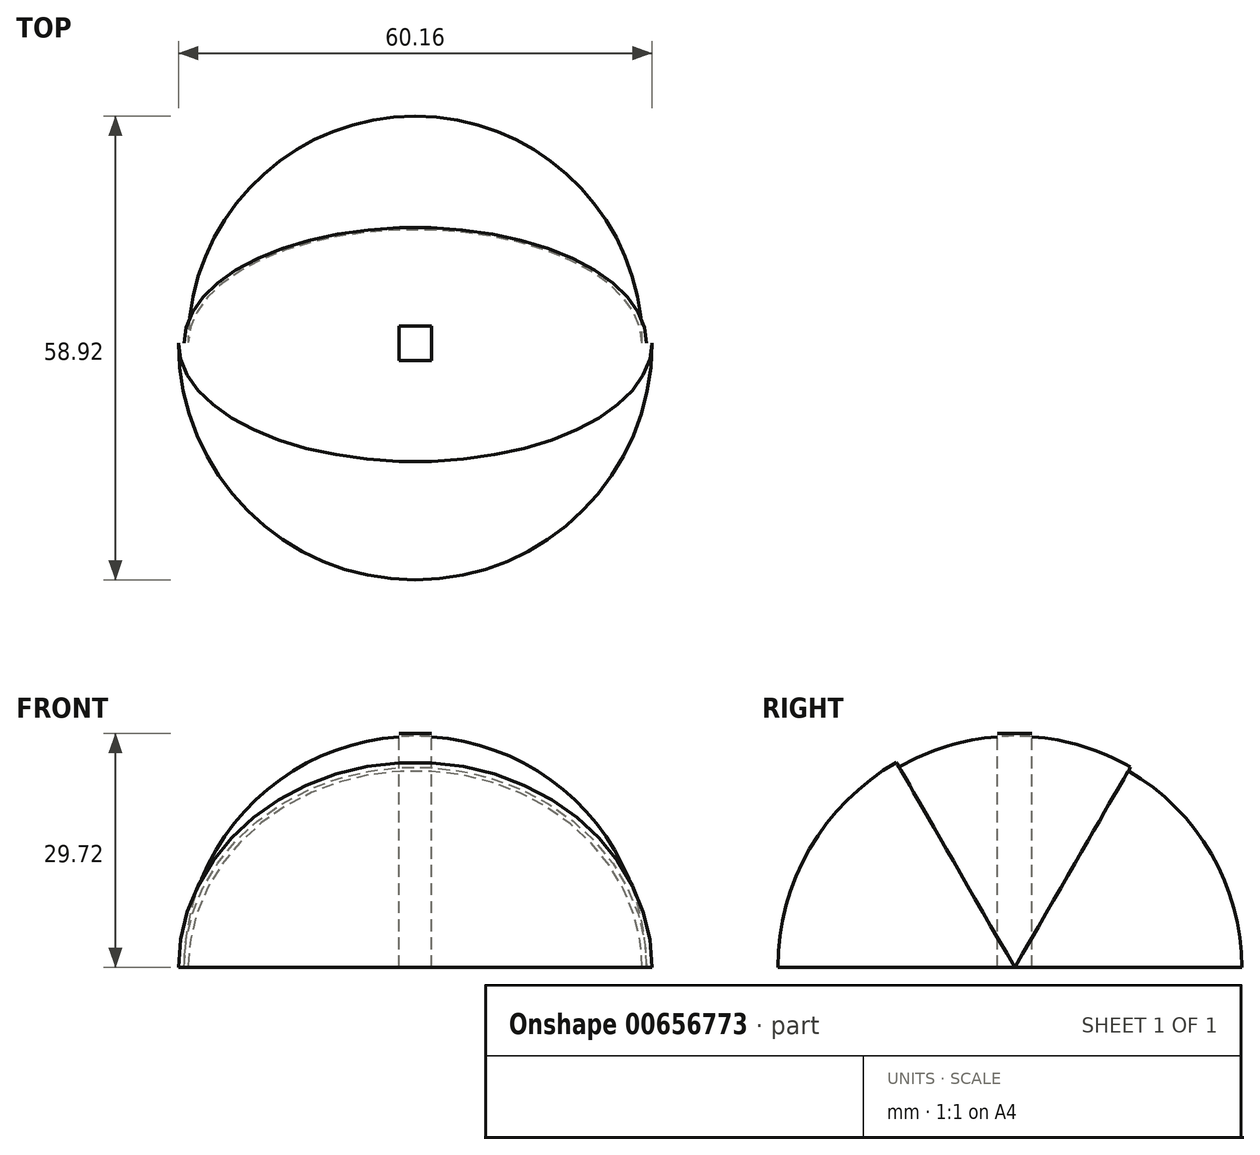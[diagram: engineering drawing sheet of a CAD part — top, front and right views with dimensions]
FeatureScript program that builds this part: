
annotation { "Feature Type Name" : "Feature", "Feature Type Description" : "" }
export const myFeature = defineFeature(function(context is Context, id is Id, definition is map)
    precondition{}
    {
        {
            var Q0;
            Q0=qCreatedBy(makeId("Top.planeOp"),FACE);
            var sketch = newSketch(context, id + "F0", { "sketchPlane" : qUnion([Q0])});
            skArc(sketch, "E0", {"start": v(-30.08, 0) * mm, "mid": v(0, -30.08) * mm, "end": v(30.08, 0) * mm});
            skLineSegment(sketch, "E1", {"start": v(30.08, 0) * mm, "end": v(-30.08, 0) * mm});
            skSolve(sketch);
        }
        {
            var Q0;
            Q0 = qSketchRegion(id + "F0", true);
            var Q1;
            Q1=sQuery(id+"F0.wireOp",EDGE,"E0");
            var Q2;
            Q2 = qBodyType(qCreatedBy(id + "F9tb82EHwottTsZ_0" ,EDGE), BodyType.WIRE);
            var Q3;
            Q3=sQuery(id+"F0.wireOp",EDGE,"E1");
            revolve(context, id + "F1", {"bodyType" : ToolBodyType.SURFACE, "entities" : qUnion([Q0]), "surfaceEntities" : qUnion([Q1, Q2]), "axis" : qUnion([Q3]), "revolveType" : RevolveType.ONE_DIRECTION, "angle" : 60 * degree});
        }
        {
            var Q0;
            Q0=qCreatedBy(makeId("Top.planeOp"),FACE);
            var sketch = newSketch(context, id + "F2", { "sketchPlane" : qUnion([Q0])});
            skArc(sketch, "E2", {"start": v(28.84, 0) * mm, "mid": v(0.1, 28.84) * mm, "end": v(-28.84, 0.2) * mm});
            skLineSegment(sketch, "E3", {"start": v(-28.84, 0.2) * mm, "end": v(28.84, 0) * mm});
            skSolve(sketch);
        }
        {
            var Q0;
            Q0=makeQuery(id+"F2.imprint","IMPRINT",FACE,{"disambiguationData":[TD([[makeQuery(id+"F2.imprint","IMPRINT",EDGE,{"derivedFrom":sQuery(id+"F2.wireOp",EDGE,"E2")}),1.0]])]});
            var Q1;
            Q1=sQuery(id+"F2.wireOp",EDGE,"E2");
            var Q2;
            Q2=sQuery(id+"F0.wireOp",EDGE,"E1");
            revolve(context, id + "F3", {"bodyType" : ToolBodyType.SURFACE, "entities" : qUnion([Q0]), "surfaceEntities" : qUnion([Q1]), "axis" : qUnion([Q2]), "revolveType" : RevolveType.ONE_DIRECTION, "oppositeDirection" : true, "angle" : 60 * degree});
        }
        {
            var Q0;
            Q0=qCreatedBy(makeId("Top.planeOp"),FACE);
            var sketch = newSketch(context, id + "F4", { "sketchPlane" : qUnion([Q0])});
            skLineSegment(sketch, "E4", {"start": v(29.67, 0) * mm, "end": v(-29.38, 0) * mm});
            skArc(sketch, "E5", {"start": v(-29.38, 0) * mm, "mid": v(0, -29.38) * mm, "end": v(29.38, 0) * mm});
            skSolve(sketch);
        }
        {
            var Q0;
            Q0 = qSketchRegion(id + "F4", true);
            var Q1;
            Q1=sQuery(id+"F4.wireOp",EDGE,"E5");
            var Q2;
            Q2=sQuery(id+"F0.wireOp",EDGE,"E1");
            revolve(context, id + "F5", {"bodyType" : ToolBodyType.SURFACE, "entities" : qUnion([Q0]), "surfaceEntities" : qUnion([Q1]), "axis" : qUnion([Q2]), "revolveType" : RevolveType.TWO_DIRECTIONS, "angle" : 120 * degree, "angleBack" : 60 * degree});
        }
        {
            var Q0;
            Q0=qCreatedBy(makeId("Top.planeOp"),FACE);
            var sketch = newSketch(context, id + "F6", { "sketchPlane" : qUnion([Q0])});
            skLineSegment(sketch, "E6.bottom", {"start": v(2.08, 2.18) * mm, "end": v(-2.08, 2.18) * mm});
            skLineSegment(sketch, "E6.top", {"start": v(2.08, -2.18) * mm, "end": v(-2.08, -2.18) * mm});
            skLineSegment(sketch, "E6.left", {"start": v(2.08, 2.18) * mm, "end": v(2.08, -2.18) * mm});
            skLineSegment(sketch, "E6.right", {"start": v(-2.08, 2.18) * mm, "end": v(-2.08, -2.18) * mm});
            skPoint(sketch, "E6.middle", {"position": v(0, 0) * mm});
            skSolve(sketch);
        }
        {
            var Q0;
            Q0 = qSketchRegion(id + "F6", true);
            var Q1;
            Q1 = qBodyType(qCreatedBy(id + "F6" ,EDGE), BodyType.WIRE);
            extrude(context, id + "F7", {"entities" : qUnion([Q0]), "bodyType" : ToolBodyType.SURFACE, "surfaceEntities" : qUnion([Q1]), "depth" : 29.72 * mm, "offsetDistance" : 25.4 * mm});
        }
    });
